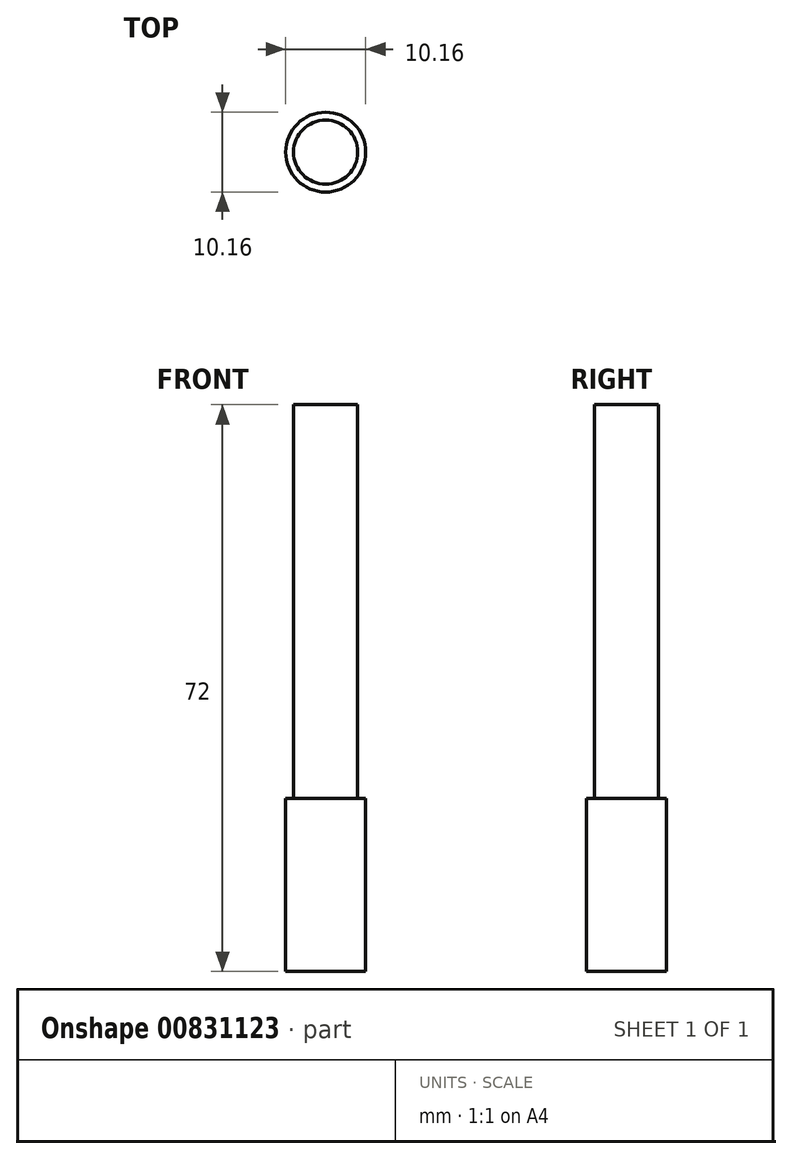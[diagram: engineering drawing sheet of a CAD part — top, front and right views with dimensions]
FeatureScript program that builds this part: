
annotation { "Feature Type Name" : "Feature", "Feature Type Description" : "" }
export const myFeature = defineFeature(function(context is Context, id is Id, definition is map)
    precondition{}
    {
        {
            var Q0;
            Q0=qCreatedBy(makeId("Front.planeOp"),FACE);
            var sketch = newSketch(context, id + "F0", { "sketchPlane" : qUnion([Q0])});
            skLineSegment(sketch, "E0", {"start": v(0, 0) * mm, "end": v(4.08, 0) * mm});
            skLineSegment(sketch, "E1", {"start": v(4.08, 0) * mm, "end": v(4.08, -50) * mm});
            skLineSegment(sketch, "E2", {"start": v(4.08, -50) * mm, "end": v(5.08, -50) * mm});
            skLineSegment(sketch, "E3", {"start": v(5.08, -50) * mm, "end": v(5.08, -72) * mm});
            skLineSegment(sketch, "E4", {"start": v(5.08, -72) * mm, "end": v(0, -72) * mm});
            skLineSegment(sketch, "E5", {"start": v(0, -72) * mm, "end": v(0, 0) * mm});
            skSolve(sketch);
        }
        {
            var Q0;
            Q0=makeQuery(id+"F0.imprint","IMPRINT",FACE,{"disambiguationData":[TD([[makeQuery(id+"F0.imprint","IMPRINT",EDGE,{"derivedFrom":sQuery(id+"F0.wireOp",EDGE,"E0")}),-1.0]])]});
            var Q1;
            Q1=sQuery(id+"F0.wireOp",EDGE,"E5");
            revolve(context, id + "F1", {"surfaceOperationType" : NewSurfaceOperationType.NEW, "entities" : qUnion([Q0]), "axis" : qUnion([Q1]), "revolveType" : RevolveType.FULL});
        }
    });
